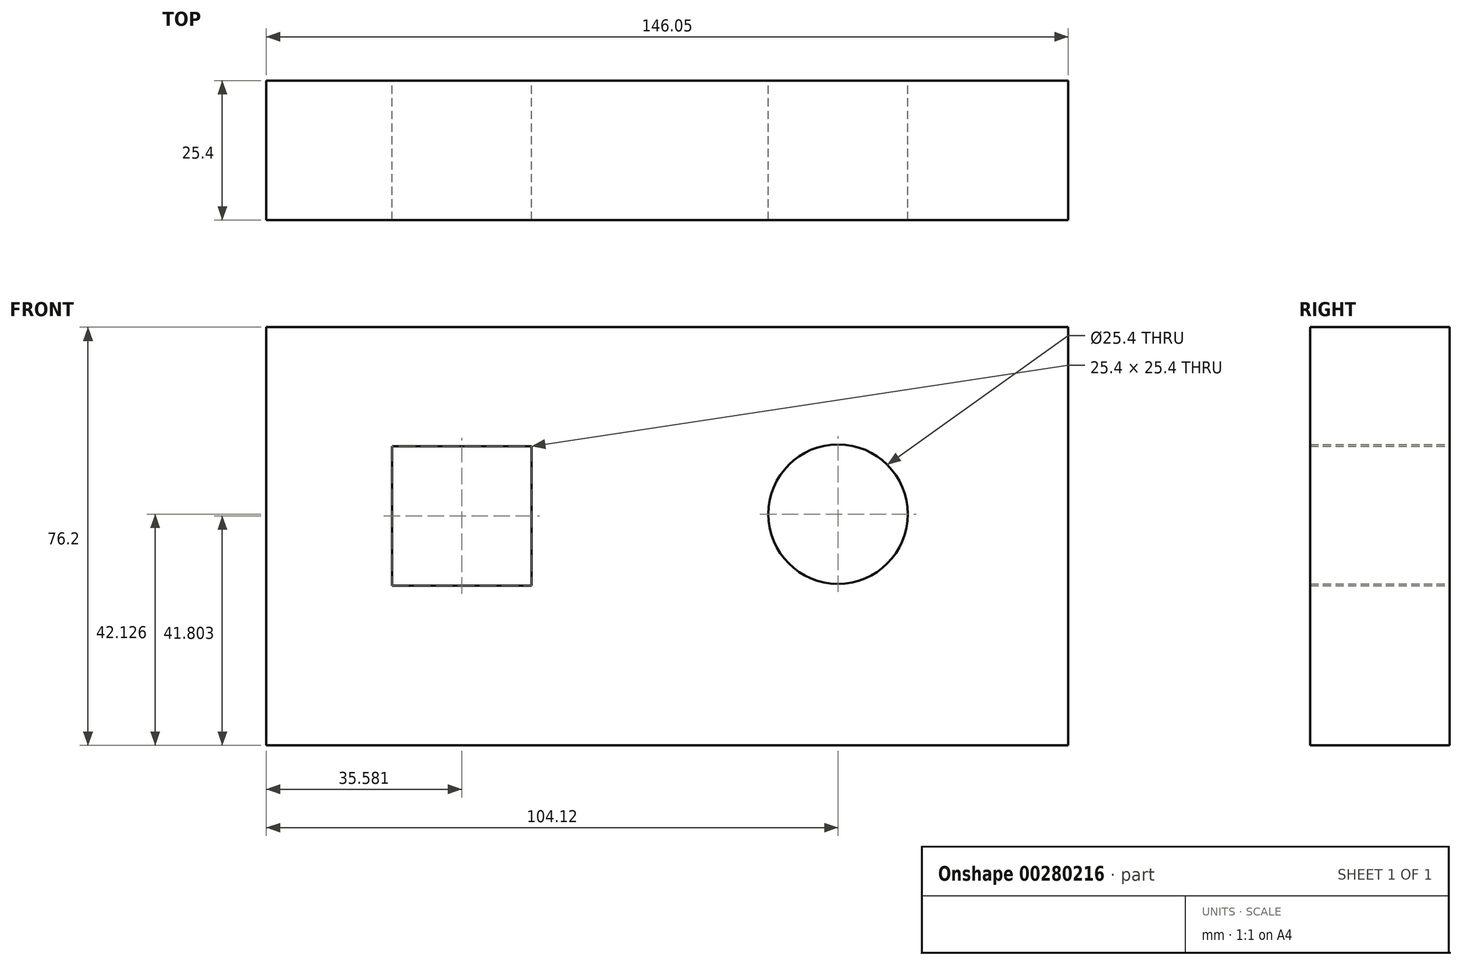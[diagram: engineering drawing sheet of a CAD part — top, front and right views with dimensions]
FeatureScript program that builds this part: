
annotation { "Feature Type Name" : "Feature", "Feature Type Description" : "" }
export const myFeature = defineFeature(function(context is Context, id is Id, definition is map)
    precondition{}
    {
        {
            var Q0;
            Q0=qCreatedBy(makeId("Front.planeOp"),FACE);
            var sketch = newSketch(context, id + "F0", { "sketchPlane" : qUnion([Q0])});
            skLineSegment(sketch, "E0.bottom", {"start": v(0, 0) * mm, "end": v(-146.05, 0) * mm});
            skLineSegment(sketch, "E0.top", {"start": v(0, 76.2) * mm, "end": v(-146.05, 76.2) * mm});
            skLineSegment(sketch, "E0.left", {"start": v(0, 0) * mm, "end": v(0, 76.2) * mm});
            skLineSegment(sketch, "E0.right", {"start": v(-146.05, 0) * mm, "end": v(-146.05, 76.2) * mm});
            skLineSegment(sketch, "E1.bottom", {"start": v(-123.17, 54.5) * mm, "end": v(-97.77, 54.5) * mm});
            skLineSegment(sketch, "E1.top", {"start": v(-123.17, 29.1) * mm, "end": v(-97.77, 29.1) * mm});
            skLineSegment(sketch, "E1.left", {"start": v(-123.17, 54.5) * mm, "end": v(-123.17, 29.1) * mm});
            skLineSegment(sketch, "E1.right", {"start": v(-97.77, 54.5) * mm, "end": v(-97.77, 29.1) * mm});
            skCircle(sketch, "E2", {"center": v(-41.93, 42.13) * mm, "radius": 12.7 * mm});
            skSolve(sketch);
        }
        {
            var Q0;
            Q0=makeQuery(id+"F0.imprint","IMPRINT",FACE,{"disambiguationData":[TD([[makeQuery(id+"F0.imprint","IMPRINT",EDGE,{"derivedFrom":sQuery(id+"F0.wireOp",EDGE,"E0.bottom")}),-1.0]])]});
            extrude(context, id + "F1", {"entities" : qUnion([Q0]), "depth" : 25.4 * mm});
        }
    });
